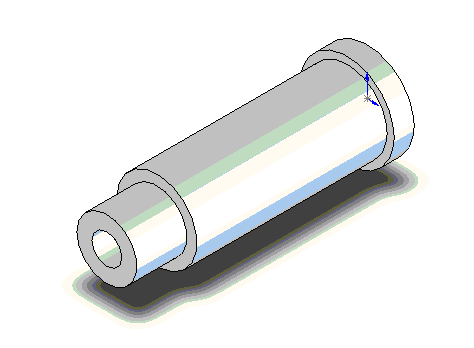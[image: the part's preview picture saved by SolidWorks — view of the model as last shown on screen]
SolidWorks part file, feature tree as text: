
SOLIDWORKS PART (.sldprt)
format: sldprt  version: not decoded by parser v0  size: 101,376 bytes
history: native  units: mm
features: sketch x4, extrude x3, material x1, cut_extrude x1 (+15 scaffold rows collapsed)
feature tree (24):
  scaffold x15  (default folders/planes/origin — collapsed)
  material  "Material <not specified>"
  sketch  "Sketch1"  dims[D1=~7.099516mm]
  extrude  "Extrude1"  Depth=2mm
  sketch  "Sketch2"  dims[D1=3.175mm]
  extrude  "Extrude2"  Depth=19mm
  sketch  "Sketch3"  dims[D1=3.175mm]
  extrude  "Extrude3"  Depth=5mm
  sketch  "Sketch4"  dims[D1=3.175mm]
  cut_extrude  "Cut-Extrude1"  [1 undecoded]
decode coverage: 7 of 8 modeling features carry decoded parameters
note: ~ marks probable driven/reference dimensions
note: 1 parameter value undecoded
note: suppression state not decoded; provenance and decode notes live in map.json
